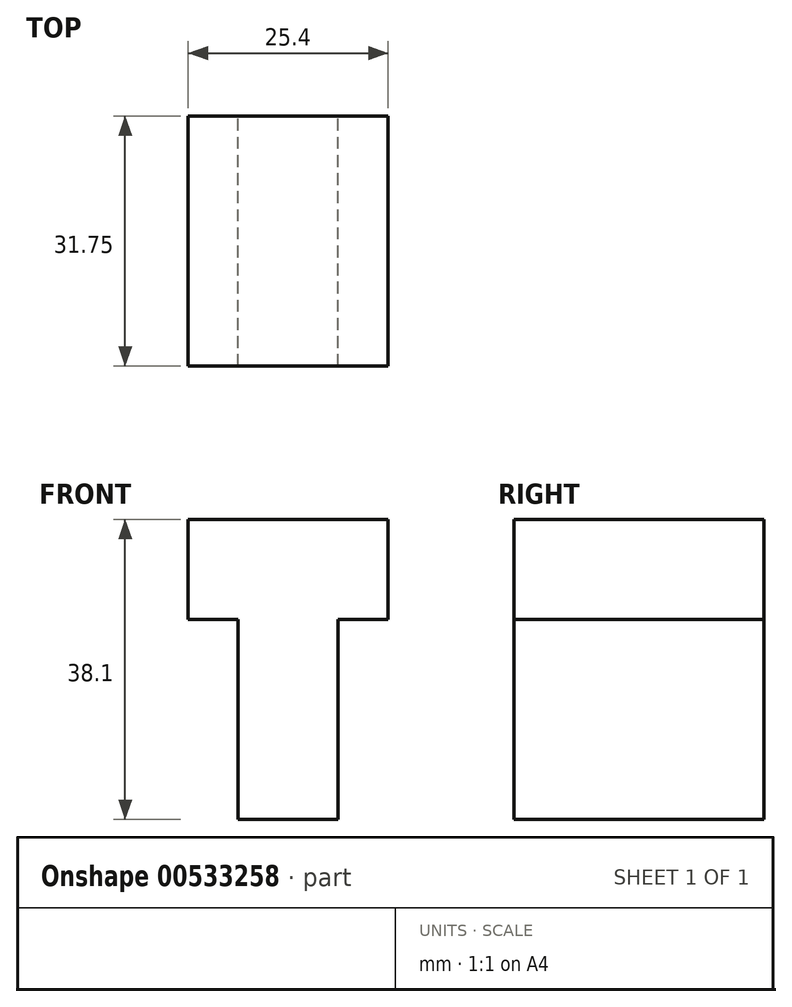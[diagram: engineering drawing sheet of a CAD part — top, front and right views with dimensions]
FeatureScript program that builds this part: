
annotation { "Feature Type Name" : "Feature", "Feature Type Description" : "" }
export const myFeature = defineFeature(function(context is Context, id is Id, definition is map)
    precondition{}
    {
        {
            var Q0;
            Q0=qCreatedBy(makeId("Front.planeOp"),FACE);
            var sketch = newSketch(context, id + "F0", { "sketchPlane" : qUnion([Q0])});
            skLineSegment(sketch, "E0", {"start": v(-59.46, 50.66) * mm, "end": v(-59.46, 37.96) * mm});
            skLineSegment(sketch, "E1", {"start": v(-59.46, 37.96) * mm, "end": v(-53.11, 37.96) * mm});
            skLineSegment(sketch, "E2", {"start": v(-53.11, 37.96) * mm, "end": v(-53.11, 12.56) * mm});
            skLineSegment(sketch, "E3", {"start": v(-53.11, 12.56) * mm, "end": v(-40.41, 12.56) * mm});
            skLineSegment(sketch, "E4", {"start": v(-40.41, 12.56) * mm, "end": v(-40.41, 37.96) * mm});
            skLineSegment(sketch, "E5", {"start": v(-40.41, 37.96) * mm, "end": v(-34.06, 37.96) * mm});
            skLineSegment(sketch, "E6", {"start": v(-34.06, 37.96) * mm, "end": v(-34.06, 50.66) * mm});
            skLineSegment(sketch, "E7", {"start": v(-34.06, 50.66) * mm, "end": v(-59.46, 50.66) * mm});
            skSolve(sketch);
        }
        {
            var Q0;
            Q0=makeQuery(id+"F0.imprint","IMPRINT",FACE,{"disambiguationData":[TD([[makeQuery(id+"F0.imprint","IMPRINT",EDGE,{"derivedFrom":sQuery(id+"F0.wireOp",EDGE,"E0")}),1.0]])]});
            extrude(context, id + "F1", {"entities" : qUnion([Q0]), "depth" : 31.75 * mm, "offsetDistance" : 25.4 * mm});
        }
    });
